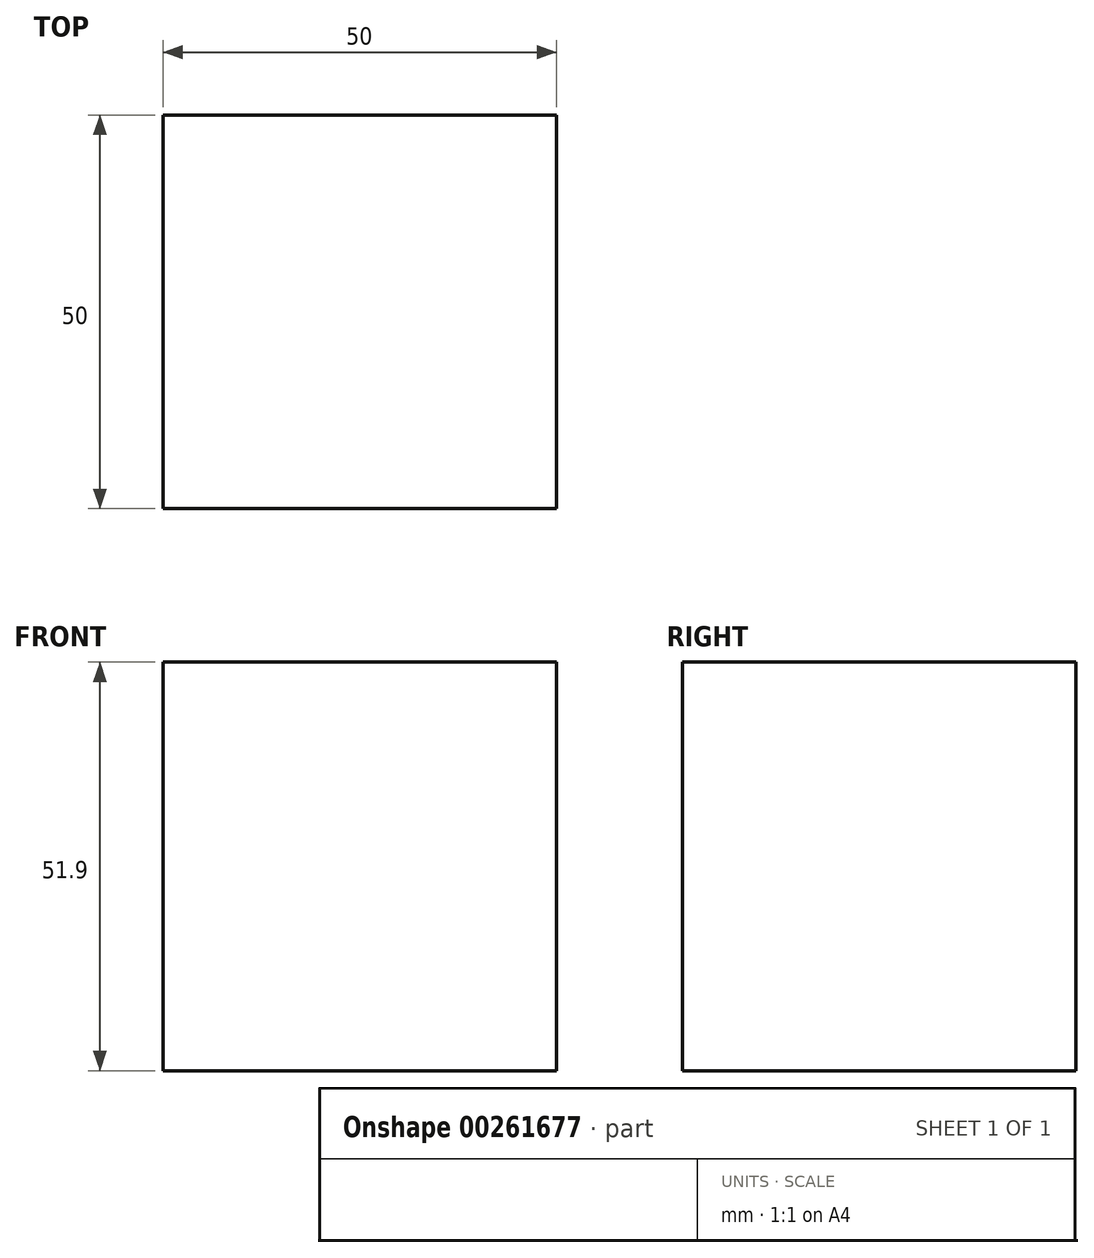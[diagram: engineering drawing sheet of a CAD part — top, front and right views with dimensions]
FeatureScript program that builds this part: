
annotation { "Feature Type Name" : "Feature", "Feature Type Description" : "" }
export const myFeature = defineFeature(function(context is Context, id is Id, definition is map)
    precondition{}
    {
        {
            var Q0;
            Q0=qCreatedBy(makeId("Top.planeOp"),FACE);
            var sketch = newSketch(context, id + "F0", { "sketchPlane" : qUnion([Q0])});
            skLineSegment(sketch, "E0.bottom", {"start": v(-25, 25) * mm, "end": v(25, 25) * mm});
            skLineSegment(sketch, "E0.top", {"start": v(-25, -25) * mm, "end": v(25, -25) * mm});
            skLineSegment(sketch, "E0.left", {"start": v(-25, 25) * mm, "end": v(-25, -25) * mm});
            skLineSegment(sketch, "E0.right", {"start": v(25, 25) * mm, "end": v(25, -25) * mm});
            skSolve(sketch);
        }
        {
            var Q0;
            Q0=makeQuery(id+"F0.imprint","IMPRINT",FACE,{"disambiguationData":[TD([[makeQuery(id+"F0.imprint","IMPRINT",EDGE,{"derivedFrom":sQuery(id+"F0.wireOp",EDGE,"E0.bottom")}),-1.0]])]});
            extrude(context, id + "F1", {"entities" : qUnion([Q0]), "depth" : 51.9 * mm});
        }
    });
